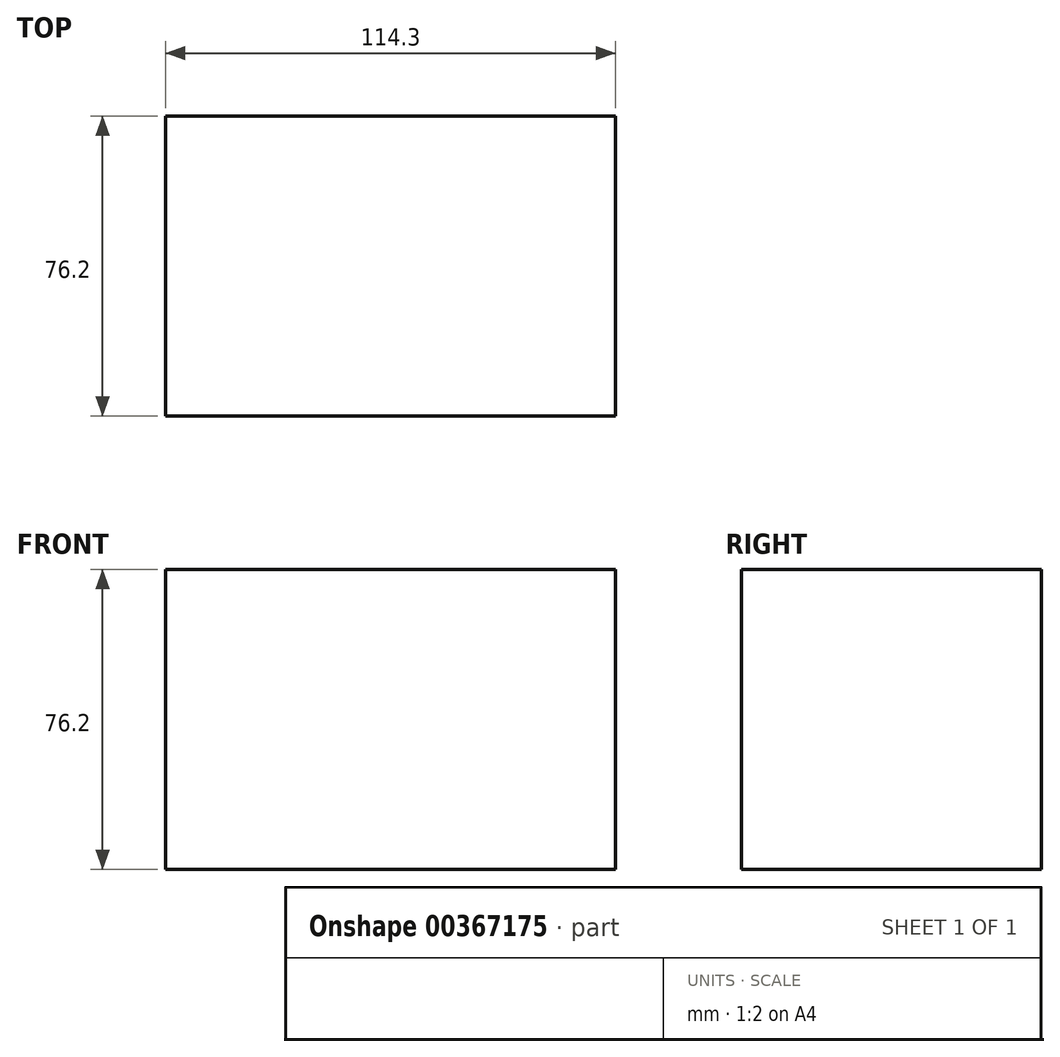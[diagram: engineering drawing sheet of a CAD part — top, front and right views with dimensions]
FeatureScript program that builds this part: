
annotation { "Feature Type Name" : "Feature", "Feature Type Description" : "" }
export const myFeature = defineFeature(function(context is Context, id is Id, definition is map)
    precondition{}
    {
        {
            var Q0;
            Q0=qCreatedBy(makeId("Front.planeOp"),FACE);
            var sketch = newSketch(context, id + "F0", { "sketchPlane" : qUnion([Q0])});
            skLineSegment(sketch, "E0.bottom", {"start": v(-19.31, 44.5) * mm, "end": v(94.99, 44.5) * mm});
            skLineSegment(sketch, "E0.top", {"start": v(-19.31, -31.7) * mm, "end": v(94.99, -31.7) * mm});
            skLineSegment(sketch, "E0.left", {"start": v(-19.31, 44.5) * mm, "end": v(-19.31, -31.7) * mm});
            skLineSegment(sketch, "E0.right", {"start": v(94.99, 44.5) * mm, "end": v(94.99, -31.7) * mm});
            skSolve(sketch);
        }
        {
            var Q0;
            Q0 = qSketchRegion(id + "F0", true);
            extrude(context, id + "F1", {"entities" : qUnion([Q0]), "depth" : 76.2 * mm});
        }
    });
